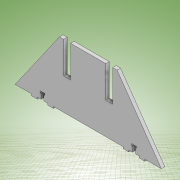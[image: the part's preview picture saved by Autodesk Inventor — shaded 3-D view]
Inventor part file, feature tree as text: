
AUTODESK INVENTOR PART (.ipt)
format: ipt  version: 2022 (Build 260153000, 153)  size: 187,904 bytes
history: native  units: mm
features: extrude x3, sketch x2, other x1
ambient origin geometry x8: Origin, YZ Plane, XZ Plane, XY Plane, X Axis, Y Axis, Z Axis, Center Point
bodies: Body1 (feature_tree)
feature tree (6):
  other  "Sólido1"
  extrude  "Extrusión1"  Depth=110.0mm
  extrude  "Extrusión3"  Depth=12.0mm
  extrude  "Extrusión4"  Depth=3.0mm
  sketch  "Boceto3"  dims[d1=100.0mm d2=110.0mm]
  sketch  "Boceto4"  dims[d3=61.0mm d5=12.0mm d6=7.5mm d7=9.599311mm d9=9.599311mm d12=55.0mm d13=6.0mm d14=0.0mm d23=9.599311mm d24=9.599311mm d25=5.0mm d26=8.0mm d27=12.0mm d29=45.0mm d30=3.0mm d31=3.0mm d32=0.0mm d33=10.0mm d34=18.0mm d35=10.0mm d36=3.0mm d37=0.0mm]
